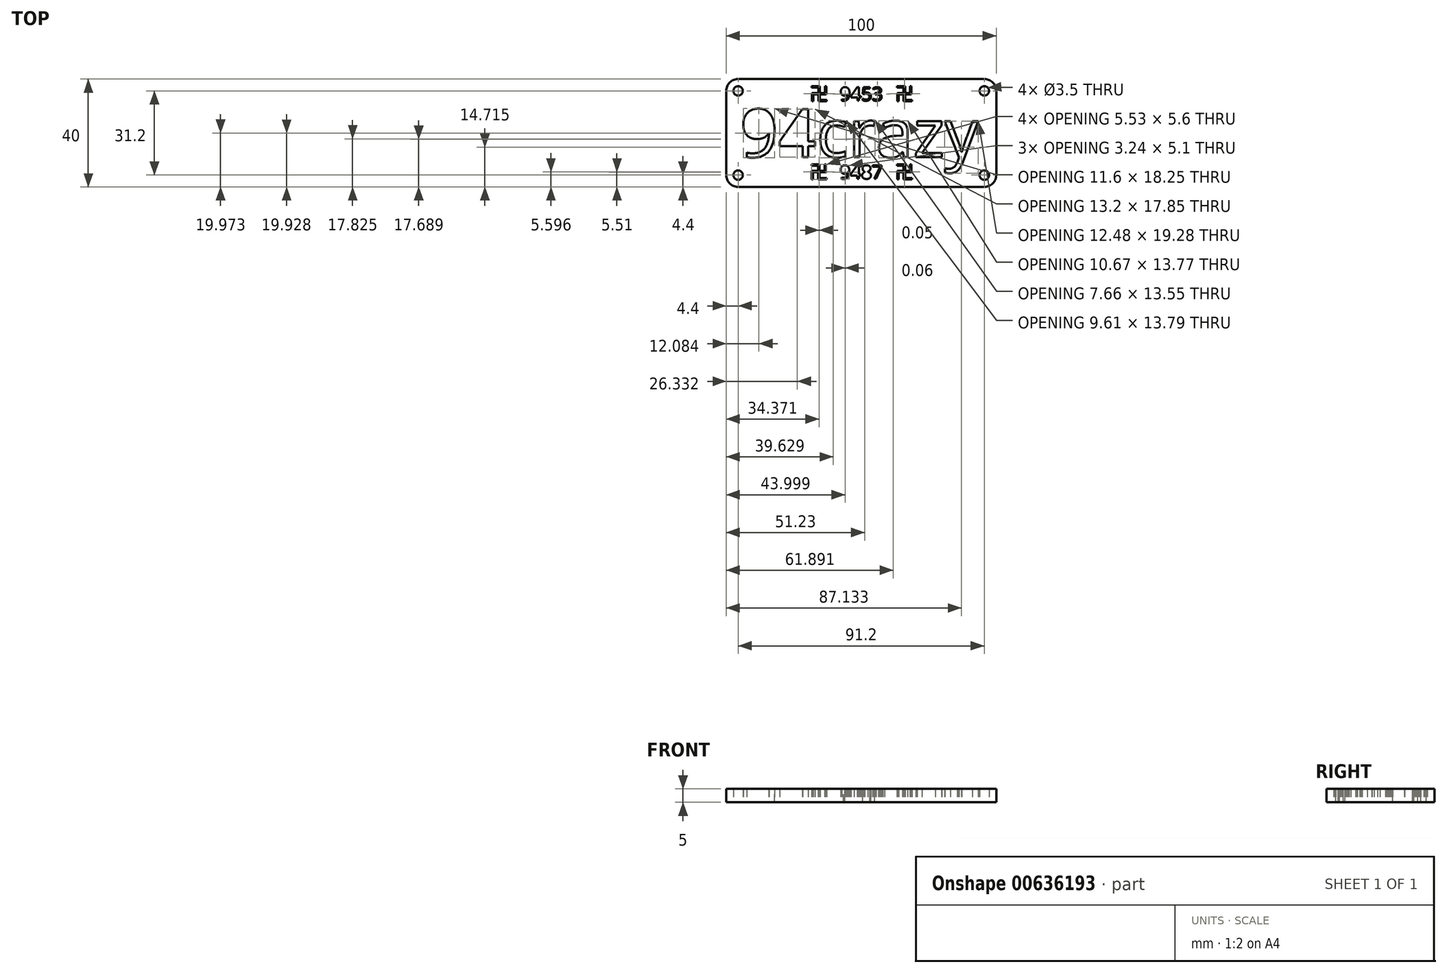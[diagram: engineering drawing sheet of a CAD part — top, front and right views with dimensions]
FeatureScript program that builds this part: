
annotation { "Feature Type Name" : "Feature", "Feature Type Description" : "" }
export const myFeature = defineFeature(function(context is Context, id is Id, definition is map)
    precondition{}
    {
        {
            var Q0;
            Q0=qCreatedBy(makeId("Top.planeOp"),FACE);
            var sketch = newSketch(context, id + "F0", { "sketchPlane" : qUnion([Q0])});
            skLineSegment(sketch, "E0.bottom", {"start": v(4.4, 0) * mm, "end": v(95.6, 0) * mm});
            skLineSegment(sketch, "E0.top", {"start": v(4.4, 40) * mm, "end": v(95.6, 40) * mm});
            skLineSegment(sketch, "E0.left", {"start": v(0, 4.4) * mm, "end": v(0, 35.6) * mm});
            skLineSegment(sketch, "E0.right", {"start": v(100, 4.4) * mm, "end": v(100, 35.6) * mm});
            skPoint(sketch, "E1.visualSharp", {"position": v(0, 40) * mm});
            skArc(sketch, "E1.filletArc", {"start": v(4.4, 40) * mm, "mid": v(1.29, 38.71) * mm, "end": v(0, 35.6) * mm});
            skPoint(sketch, "E2.visualSharp", {"position": v(0, 0) * mm});
            skArc(sketch, "E2.filletArc", {"start": v(0, 4.4) * mm, "mid": v(1.29, 1.29) * mm, "end": v(4.4, 0) * mm});
            skPoint(sketch, "E3.visualSharp", {"position": v(100, 0) * mm});
            skArc(sketch, "E3.filletArc", {"start": v(95.6, 0) * mm, "mid": v(98.71, 1.29) * mm, "end": v(100, 4.4) * mm});
            skPoint(sketch, "E4.visualSharp", {"position": v(100, 40) * mm});
            skArc(sketch, "E4.filletArc", {"start": v(100, 35.6) * mm, "mid": v(98.71, 38.71) * mm, "end": v(95.6, 40) * mm});
            skCircle(sketch, "E5", {"center": v(4.4, 35.6) * mm, "radius": 1.75 * mm});
            skCircle(sketch, "E6", {"center": v(4.4, 4.4) * mm, "radius": 1.75 * mm});
            skCircle(sketch, "E7", {"center": v(95.6, 4.4) * mm, "radius": 1.75 * mm});
            skCircle(sketch, "E8", {"center": v(95.6, 35.6) * mm, "radius": 1.75 * mm});
            skText(sketch, "E9", { "text": "94crazy", "fontName": "OpenSans-Regular.ttf"});
            skText(sketch, "E10", { "text": "9453", "fontName": "OpenSans-Regular.ttf"});
            skText(sketch, "E11", { "text": "9487", "fontName": "OpenSans-Regular.ttf"});
            skLineSegment(sketch, "E12", {"start": v(15.54, 24.51) * mm, "end": v(17.46, 24.51) * mm});
            skLineSegment(sketch, "E13", {"start": v(15.81, 23.26) * mm, "end": v(17.74, 23.26) * mm});
            skLineSegment(sketch, "E14", {"start": v(17.74, 23.26) * mm, "end": v(17.74, 23.26) * mm});
            skText(sketch, "E15", { "text": "卍", "fontName": "NotoSansCJKtc-Regular.otf"});
            skText(sketch, "E16", { "text": "卍", "fontName": "NotoSansCJKtc-Regular.otf"});
            skText(sketch, "E17", { "text": "卍", "fontName": "NotoSansCJKtc-Regular.otf"});
            skText(sketch, "E18", { "text": "卍", "fontName": "NotoSansCJKtc-Regular.otf"});
            const initialGuessF0  = {"E9": [0.005, 0.01105, 1, 0, 0.0179], "E10": [0.04208, 0.03198, 1, 0, 0.005], "E11": [0.04202, 0.00303, 1, 0, 0.005], "E15": [0.0309, 0.03198, 1, 0, 0.005], "E16": [0.0625, 0.03198, 1, 0, 0.005], "E17": [0.0625, 0.00303, 1, 0, 0.005], "E18": [0.03085, 0.00303, 1, 0, 0.005]};
            skSetInitialGuess(sketch, initialGuessF0);
            skSolve(sketch);
        }
        {
            var Q0;
            Q0 = qSketchRegion(id + "F0", true);
            extrude(context, id + "F1", {"entities" : qUnion([Q0]), "depth" : 5 * mm, "offsetDistance" : 25 * mm});
        }
    });
